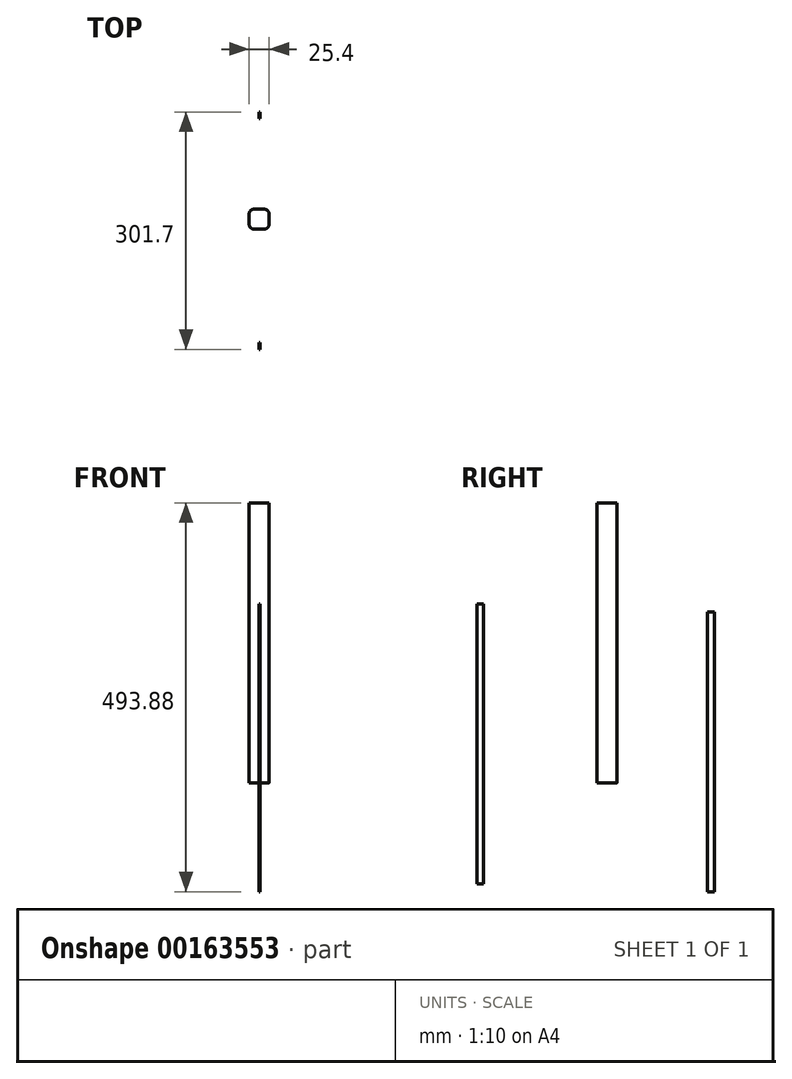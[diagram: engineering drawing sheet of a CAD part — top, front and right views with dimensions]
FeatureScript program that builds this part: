
annotation { "Feature Type Name" : "Feature", "Feature Type Description" : "" }
export const myFeature = defineFeature(function(context is Context, id is Id, definition is map)
    precondition{}
    {
        {
            var Q0;
            Q0=qCreatedBy(makeId("Top.planeOp"),FACE);
            var sketch = newSketch(context, id + "F0", { "sketchPlane" : qUnion([Q0])});
            skLineSegment(sketch, "E0.bottom", {"start": v(6.35, 12.7) * mm, "end": v(-6.35, 12.7) * mm});
            skLineSegment(sketch, "E0.top", {"start": v(6.35, -12.7) * mm, "end": v(-6.35, -12.7) * mm});
            skLineSegment(sketch, "E0.left", {"start": v(12.7, 6.35) * mm, "end": v(12.7, -6.35) * mm});
            skLineSegment(sketch, "E0.right", {"start": v(-12.7, 6.35) * mm, "end": v(-12.7, -6.35) * mm});
            skPoint(sketch, "E0.middle", {"position": v(0, 0) * mm});
            skPoint(sketch, "E1.visualSharp", {"position": v(-12.7, 12.7) * mm});
            skArc(sketch, "E1.filletArc", {"start": v(-6.35, 12.7) * mm, "mid": v(-10.84, 10.84) * mm, "end": v(-12.7, 6.35) * mm});
            skPoint(sketch, "E2.visualSharp", {"position": v(-12.7, -12.7) * mm});
            skArc(sketch, "E2.filletArc", {"start": v(-12.7, -6.35) * mm, "mid": v(-10.84, -10.84) * mm, "end": v(-6.35, -12.7) * mm});
            skPoint(sketch, "E3.visualSharp", {"position": v(12.7, -12.7) * mm});
            skArc(sketch, "E3.filletArc", {"start": v(6.35, -12.7) * mm, "mid": v(10.84, -10.84) * mm, "end": v(12.7, -6.35) * mm});
            skPoint(sketch, "E4.visualSharp", {"position": v(12.7, 12.7) * mm});
            skArc(sketch, "E4.filletArc", {"start": v(12.7, 6.35) * mm, "mid": v(10.84, 10.84) * mm, "end": v(6.35, 12.7) * mm});
            skSolve(sketch);
        }
        {
            var Q0;
            Q0 = qSketchRegion(id + "F0", true);
            extrude(context, id + "F1", {"entities" : qUnion([Q0]), "depth" : 355.6 * mm});
        }
        {
            var Q0;
            Q0=qCreatedBy(makeId("Right.planeOp"),FACE);
            var sketch = newSketch(context, id + "F2", { "sketchPlane" : qUnion([Q0])});
            skLineSegment(sketch, "E5.bottom", {"start": v(-165.43, 227.1) * mm, "end": v(-156.96, 227.1) * mm});
            skLineSegment(sketch, "E5.top", {"start": v(-165.43, -128.5) * mm, "end": v(-156.96, -128.5) * mm});
            skLineSegment(sketch, "E5.left", {"start": v(-165.43, 227.1) * mm, "end": v(-165.43, -128.5) * mm});
            skLineSegment(sketch, "E5.right", {"start": v(-156.96, 227.1) * mm, "end": v(-156.96, -128.5) * mm});
            skSolve(sketch);
        }
        {
            var Q0;
            Q0 = qSketchRegion(id + "F2", true);
            extrude(context, id + "F3", {"entities" : qUnion([Q0]), "depth" : 1.27 * mm});
        }
        {
            var Q0;
            Q0=qCreatedBy(makeId("Right.planeOp"),FACE);
            var sketch = newSketch(context, id + "F4", { "sketchPlane" : qUnion([Q0])});
            skLineSegment(sketch, "E6.bottom", {"start": v(127.8, 217.32) * mm, "end": v(136.27, 217.32) * mm});
            skLineSegment(sketch, "E6.top", {"start": v(127.8, -138.28) * mm, "end": v(136.27, -138.28) * mm});
            skLineSegment(sketch, "E6.left", {"start": v(127.8, 217.32) * mm, "end": v(127.8, -138.28) * mm});
            skLineSegment(sketch, "E6.right", {"start": v(136.27, 217.32) * mm, "end": v(136.27, -138.28) * mm});
            skSolve(sketch);
        }
        {
            var Q0;
            Q0 = qSketchRegion(id + "F4", true);
            extrude(context, id + "F5", {"entities" : qUnion([Q0]), "depth" : 1.27 * mm});
        }
    });
